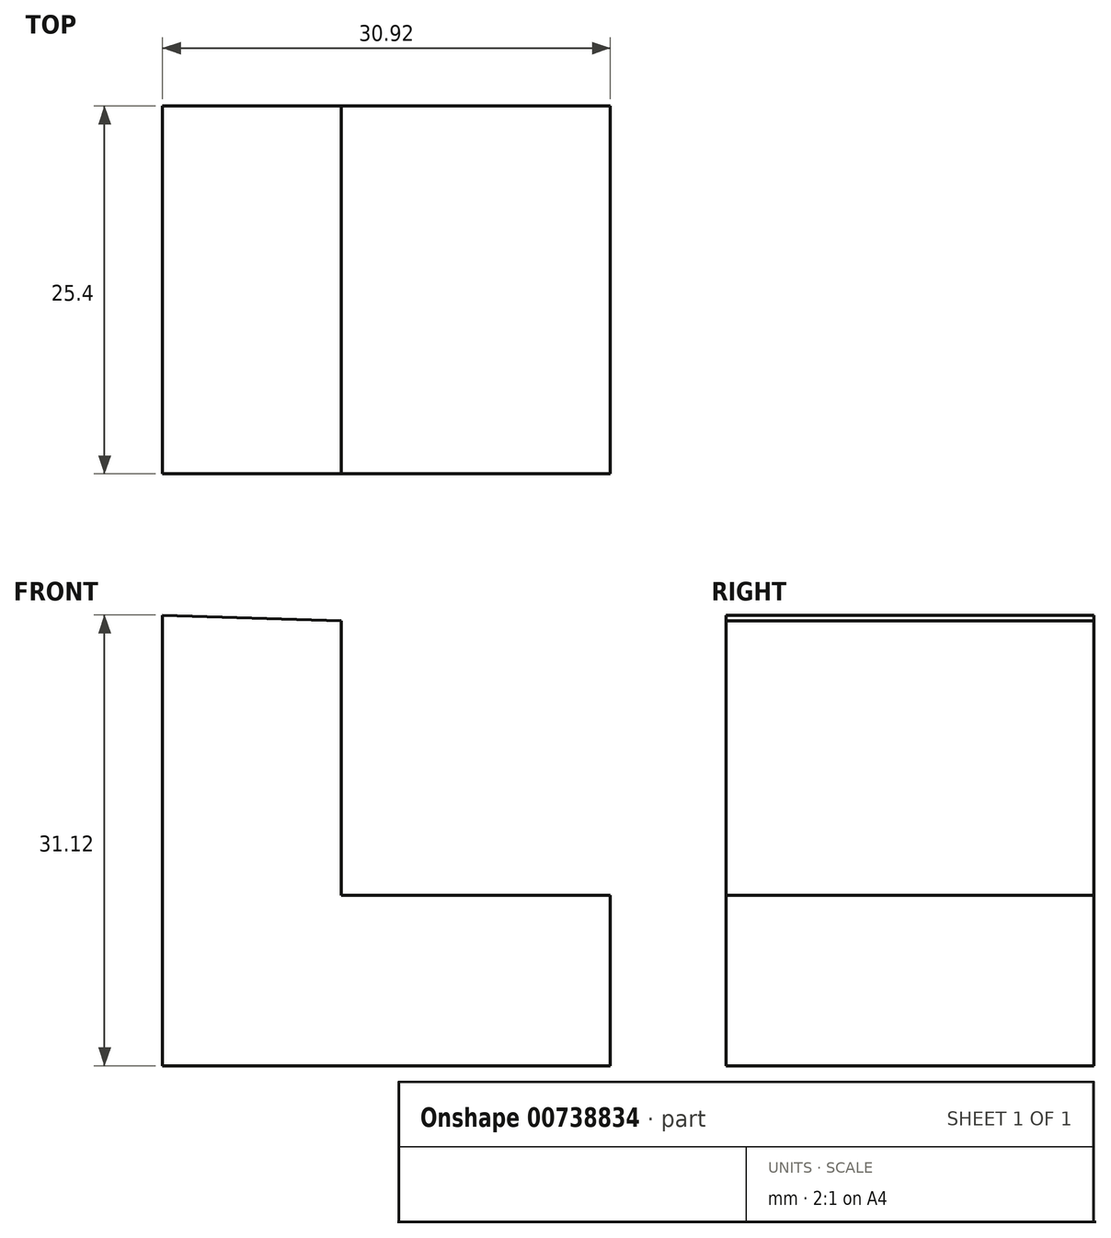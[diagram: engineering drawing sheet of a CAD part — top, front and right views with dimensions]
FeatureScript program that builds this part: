
annotation { "Feature Type Name" : "Feature", "Feature Type Description" : "" }
export const myFeature = defineFeature(function(context is Context, id is Id, definition is map)
    precondition{}
    {
        {
            var Q0;
            Q0=qCreatedBy(makeId("Front.planeOp"),FACE);
            var sketch = newSketch(context, id + "F0", { "sketchPlane" : qUnion([Q0])});
            skLineSegment(sketch, "E0", {"start": v(0, 31.12) * mm, "end": v(0, 0) * mm});
            skLineSegment(sketch, "E1", {"start": v(30.92, 0) * mm, "end": v(30.92, 11.75) * mm});
            skLineSegment(sketch, "E2", {"start": v(30.92, 11.75) * mm, "end": v(12.35, 11.75) * mm});
            skLineSegment(sketch, "E3", {"start": v(12.35, 11.75) * mm, "end": v(12.35, 30.72) * mm});
            skLineSegment(sketch, "E4", {"start": v(12.35, 30.72) * mm, "end": v(0, 31.12) * mm});
            skLineSegment(sketch, "E5", {"start": v(30.92, 0) * mm, "end": v(0, 0) * mm});
            skSolve(sketch);
        }
        {
            var Q0;
            Q0 = qSketchRegion(id + "F0", true);
            extrude(context, id + "F1", {"entities" : qUnion([Q0]), "depth" : 25.4 * mm, "offsetDistance" : 25.4 * mm});
        }
    });
